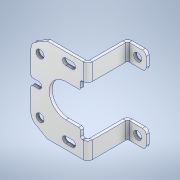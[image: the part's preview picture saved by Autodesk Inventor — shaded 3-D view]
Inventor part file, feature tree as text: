
AUTODESK INVENTOR PART (.ipt)
format: ipt  version: 2020 (Build 240168000, 168)  size: 300,032 bytes
history: native  units: mm
features: sheet_metal_op x8, sketch x4, fillet x3, other x3, hole x2, extrude x2, plane x2, projected_geometry x2
ambient origin geometry x8: Origin, YZ Plane, XZ Plane, XY Plane, X Axis, Y Axis, Z Axis, Center Point
bodies: Solid1 (feature_tree)
feature tree (26):
  sketch  "Sketch1"  dims[d0=15.0mm d1=10.0mm]
  sheet_metal_op  "Face1"
  hole  "Hole1"  [1 undecoded]
  extrude  "Extrusion3"  TaperAngle=120.0deg  [1 undecoded]
  plane  "Work Plane2"
  sheet_metal_op  "Flange1"
  sheet_metal_op  "Flange2"
  plane  "Work Plane1"
  extrude  "Extrusion4"  Depth=3.5mm
  fillet  "Fillet1"  Radius=18.0mm
  fillet  "Fillet2"  Radius=3.5mm
  hole  "Hole2"  [1 undecoded]
  fillet  "Fillet3"  Radius=2.0mm
  sheet_metal_op  "Unfold1"
  other  "Plate1"
  sketch  "Sketch3"  dims[d3=46.0mm d4=120.0deg]
  other  "Plate2"
  sheet_metal_op  "Bend1"
  sheet_metal_op  "Corner1"
  sketch  "Sketch4"  dims[d5=120.0deg d6=17.5mm d7=18.0mm d8=3.5mm]
  other  "Plate3"
  sheet_metal_op  "Bend2"
  sheet_metal_op  "Corner2"
  sketch  "Sketch5"  dims[d9=26.0mm d10=36.0mm d11=1.75mm d12=2.0mm d13=22.25mm d14=15.0mm d15=36.0mm d16=2.0mm d17=1.0mm d18=14.0mm d19=5.5mm d22=4.3mm d23=6.0mm d24=4.0mm d25=2.0mm d26=90.0deg d27=8.0mm d28=20.594885mm d32=1.6002mm d33=0.5mm d34=0.0mm d35=21.6125mm d36=21.6125mm d37=1.6002mm d38=0.8001mm d39=3.2004mm d40=0.889mm d41=21.6125mm d42=90.0deg d43=0.889mm d44=6.4008mm d45=1.6002mm d46=0.889mm d47=1.6002mm d48=0.8001mm d49=3.2004mm d50=0.889mm d51=12.0mm d52=90.0deg d53=0.889mm d54=6.4008mm d55=1.6002mm d56=0.889mm d57=0.0mm d58=0.0mm d59=2.0mm d60=1.0mm d61=4.3mm d62=6.0mm d63=4.0mm d64=2.0mm d65=90.0deg d66=8.0mm d67=20.594885mm d68=1.0mm]
  projected_geometry  "Projected Loop1"
  projected_geometry  "Projected Loop2"
note: 3 required parameter values undecoded (feature->parameter linkage not recoverable at this tier; creation-order binding heuristic only, values carry confidence <= 0.55)
